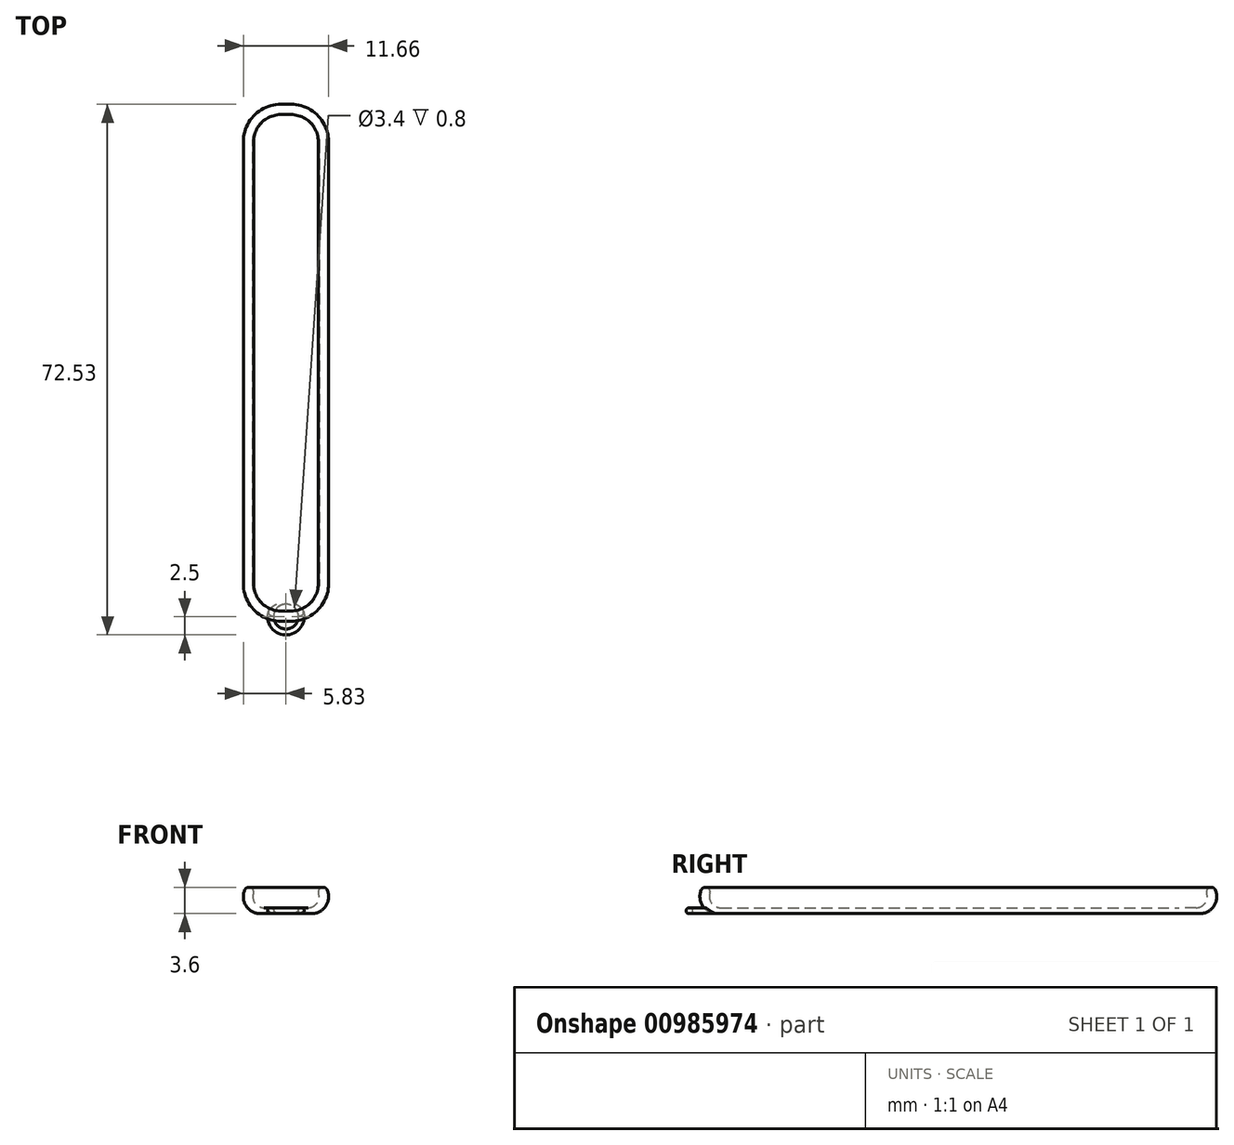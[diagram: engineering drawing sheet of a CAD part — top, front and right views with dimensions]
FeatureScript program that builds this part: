
annotation { "Feature Type Name" : "Feature", "Feature Type Description" : "" }
export const myFeature = defineFeature(function(context is Context, id is Id, definition is map)
    precondition{}
    {
        {
            var Q0;
            Q0=qCreatedBy(makeId("Front.planeOp"),FACE);
            var sketch = newSketch(context, id + "F0", { "sketchPlane" : qUnion([Q0])});
            skLineSegment(sketch, "E0", {"start": v(1.5, 0) * mm, "end": v(3.5, 0) * mm});
            skArc(sketch, "E1", {"start": v(3.5, 0) * mm, "mid": v(5.55, 1.22) * mm, "end": v(5.45, 3.6) * mm});
            skLineSegment(sketch, "E2", {"start": v(1.5, 0.8) * mm, "end": v(3, 0.8) * mm});
            skArc(sketch, "E3", {"start": v(3, 0.8) * mm, "mid": v(4.46, 1.88) * mm, "end": v(3.85, 3.6) * mm});
            skLineSegment(sketch, "E4", {"start": v(3.85, 3.6) * mm, "end": v(5.45, 3.6) * mm});
            skLineSegment(sketch, "E5", {"start": v(1.5, 0.8) * mm, "end": v(1.5, 0) * mm});
            skLineSegment(sketch, "E6", {"start": v(5.83, 5.43) * mm, "end": v(5.83, -1.68) * mm, "construction": true});
            skArc(sketch, "E7", {"start": v(5.45, 3.6) * mm, "mid": v(4.65, 4.03) * mm, "end": v(3.85, 3.6) * mm});
            skSolve(sketch);
        }
        {
            var Q0;
            Q0=qCreatedBy(makeId("Top.planeOp"),FACE);
            var sketch = newSketch(context, id + "F1", { "sketchPlane" : qUnion([Q0])});
            skLineSegment(sketch, "E8.bottom", {"start": v(0.7, -31) * mm, "end": v(-0.7, -31) * mm});
            skLineSegment(sketch, "E8.top", {"start": v(0.7, 31) * mm, "end": v(-0.7, 31) * mm});
            skLineSegment(sketch, "E8.left", {"start": v(1.5, -30.2) * mm, "end": v(1.5, 30.2) * mm});
            skLineSegment(sketch, "E8.right", {"start": v(-1.5, -30.2) * mm, "end": v(-1.5, 30.2) * mm});
            skPoint(sketch, "E8.middle", {"position": v(0, 0) * mm});
            skPoint(sketch, "E9.visualSharp", {"position": v(1.5, 31) * mm});
            skArc(sketch, "E9.filletArc", {"start": v(1.5, 30.2) * mm, "mid": v(1.27, 30.77) * mm, "end": v(0.7, 31) * mm});
            skPoint(sketch, "E10.visualSharp", {"position": v(-1.5, 31) * mm});
            skArc(sketch, "E10.filletArc", {"start": v(-0.7, 31) * mm, "mid": v(-1.27, 30.77) * mm, "end": v(-1.5, 30.2) * mm});
            skPoint(sketch, "E11.visualSharp", {"position": v(-1.5, -31) * mm});
            skArc(sketch, "E11.filletArc", {"start": v(-1.5, -30.2) * mm, "mid": v(-1.27, -30.77) * mm, "end": v(-0.7, -31) * mm});
            skPoint(sketch, "E12.visualSharp", {"position": v(1.5, -31) * mm});
            skArc(sketch, "E12.filletArc", {"start": v(0.7, -31) * mm, "mid": v(1.27, -30.77) * mm, "end": v(1.5, -30.2) * mm});
            skSolve(sketch);
        }
        {
            var Q0;
            Q0=makeQuery(id+"F0.imprint","IMPRINT",FACE,{"disambiguationData":[TD([[makeQuery(id+"F0.imprint","IMPRINT",EDGE,{"derivedFrom":sQuery(id+"F0.wireOp",EDGE,"E0")}),1.0]])]});
            var Q1;
            Q1=sQuery(id+"F1.wireOp",EDGE,"E8.left");
            var Q2;
            Q2=sQuery(id+"F1.wireOp",EDGE,"E12.filletArc");
            var Q3;
            Q3=sQuery(id+"F1.wireOp",EDGE,"E8.bottom");
            var Q4;
            Q4=sQuery(id+"F1.wireOp",EDGE,"E11.filletArc");
            var Q5;
            Q5=sQuery(id+"F1.wireOp",EDGE,"E8.right");
            var Q6;
            Q6=sQuery(id+"F1.wireOp",EDGE,"E10.filletArc");
            var Q7;
            Q7=sQuery(id+"F1.wireOp",EDGE,"E8.top");
            var Q8;
            Q8=sQuery(id+"F1.wireOp",EDGE,"E9.filletArc");
            sweep(context, id + "F2", {"profiles" : qUnion([Q0]), "path" : qUnion([Q1, Q2, Q3, Q4, Q5, Q6, Q7, Q8])});
        }
        {
            var Q0;
            Q0=makeQuery(id+"F1.imprint","IMPRINT",FACE,{"disambiguationData":[TD([[makeQuery(id+"F1.imprint","IMPRINT",EDGE,{"derivedFrom":sQuery(id+"F1.wireOp",EDGE,"E8.bottom")}),-1.0]])]});
            extrude(context, id + "F3", {"entities" : qUnion([Q0]), "operationType" : NewBodyOperationType.ADD, "depth" : .8 * mm, "offsetDistance" : 25 * mm});
        }
        {
            var Q0;
            Q0=makeQuery(id+"F2.opSweep","SWEPT_EDGE",EDGE,{"disambiguationData":[OSD([sQuery(id+"F0.wireOp",EDGE,"E3"),sQuery(id+"F0.wireOp",EDGE,"E4"),sQuery(id+"F0.wireOp",EDGE,"E7"),sQuery(id+"F1.wireOp",EDGE,"E8.right")])]});
            var Q1;
            Q1=makeQuery(id+"F2.opSweep","SWEPT_EDGE",EDGE,{"disambiguationData":[OSD([sQuery(id+"F0.wireOp",EDGE,"E1"),sQuery(id+"F0.wireOp",EDGE,"E4"),sQuery(id+"F0.wireOp",EDGE,"E7"),sQuery(id+"F1.wireOp",EDGE,"E11.filletArc")])]});
            fillet(context, id + "F4", {"entities" : qUnion([Q0, Q1]), "radius" : .6 * mm, "tangentPropagation" : true, "allowEdgeOverflow" : false});
        }
        {
            var Q0;
            Q0=qCreatedBy(makeId("Top.planeOp"),FACE);
            var sketch = newSketch(context, id + "F5", { "sketchPlane" : qUnion([Q0])});
            skCircle(sketch, "E13", {"center": v(0, -34.7) * mm, "radius": 2.5 * mm});
            skCircle(sketch, "E14", {"center": v(0, -34.7) * mm, "radius": 1.7 * mm});
            skSolve(sketch);
        }
        {
            var Q0;
            Q0=makeQuery(id+"F5.imprint","IMPRINT",FACE,{"disambiguationData":[TD([[makeQuery(id+"F5.imprint","IMPRINT",EDGE,{"derivedFrom":sQuery(id+"F5.wireOp",EDGE,"E13")}),1.0]])]});
            extrude(context, id + "F6", {"entities" : qUnion([Q0]), "operationType" : NewBodyOperationType.ADD, "depth" : .8 * mm, "offsetDistance" : 25 * mm});
        }
        {
            var Q0;
            Q0=makeQuery(id+"F6.opExtrude","CAP_EDGE",EDGE,{"disambiguationData":[OSD([sQuery(id+"F5.wireOp",EDGE,"E13")])],"isStart":true});
            var Q1;
            Q1=makeQuery(id+"F6.opExtrude","CAP_EDGE",EDGE,{"disambiguationData":[OSD([sQuery(id+"F5.wireOp",EDGE,"E13")])],"isStart":false});
            fillet(context, id + "F7", {"entities" : qUnion([Q0, Q1]), "radius" : .4 * mm, "tangentPropagation" : true, "allowEdgeOverflow" : false});
        }
    });
